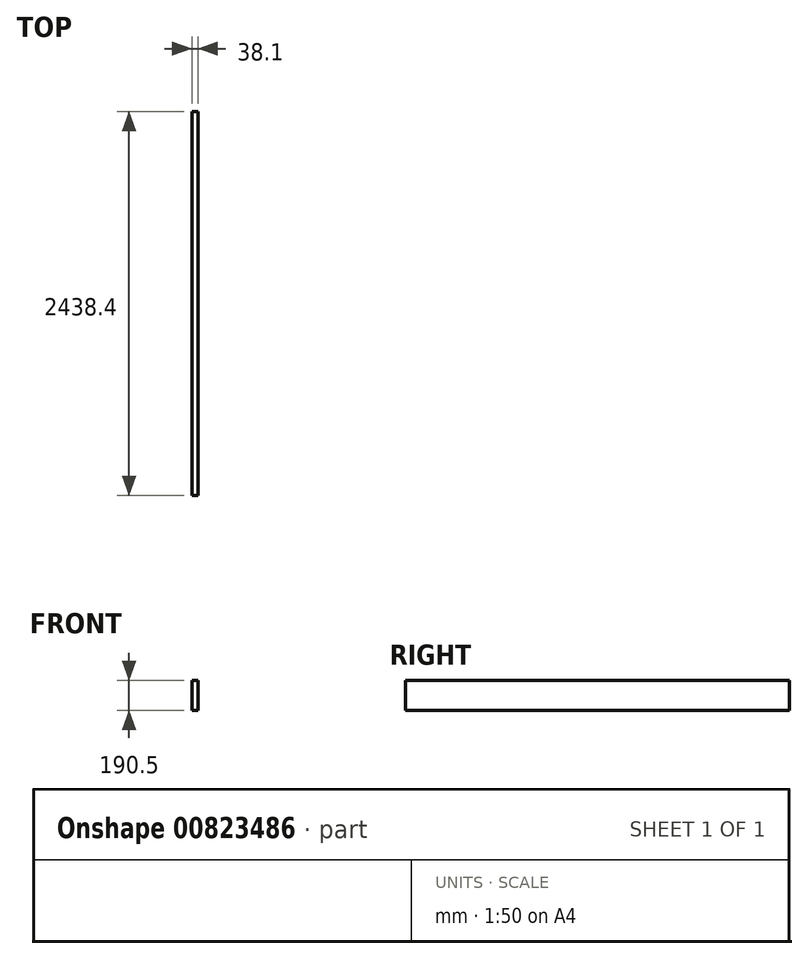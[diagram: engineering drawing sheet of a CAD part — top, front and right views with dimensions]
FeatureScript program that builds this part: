
annotation { "Feature Type Name" : "Feature", "Feature Type Description" : "" }
export const myFeature = defineFeature(function(context is Context, id is Id, definition is map)
    precondition{}
    {
        {
            var Q0;
            Q0=qCreatedBy(makeId("Front.planeOp"),FACE);
            var sketch = newSketch(context, id + "F0", { "sketchPlane" : qUnion([Q0])});
            skLineSegment(sketch, "E0.bottom", {"start": v(0, 0) * mm, "end": v(38.1, 0) * mm});
            skLineSegment(sketch, "E0.top", {"start": v(0, 190.5) * mm, "end": v(38.1, 190.5) * mm});
            skLineSegment(sketch, "E0.left", {"start": v(0, 0) * mm, "end": v(0, 190.5) * mm});
            skLineSegment(sketch, "E0.right", {"start": v(38.1, 0) * mm, "end": v(38.1, 190.5) * mm});
            skSolve(sketch);
        }
        {
            var Q0;
            Q0 = qSketchRegion(id + "F0", true);
            extrude(context, id + "F1", {"entities" : qUnion([Q0]), "depth" : 2438.4 * mm, "offsetDistance" : 25.4 * mm});
        }
    });
